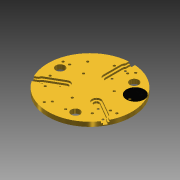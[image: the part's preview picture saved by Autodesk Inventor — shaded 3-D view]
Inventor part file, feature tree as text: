
AUTODESK INVENTOR PART (.ipt)
format: ipt  version: 2014 (Build 180170000, 170)  size: 278,528 bytes
history: native  units: in
note: dims shown in document units (in); Inventor stores cm internally (conversion verified against a paired STEP export)
features: extrude x11, sketch x11, pattern_circular x2, plane x1
ambient origin geometry x8: Origin, YZ Plane, XZ Plane, XY Plane, X Axis, Y Axis, Z Axis, Center Point
bodies: Solid1 (feature_tree)
feature tree (25):
  extrude  "Extrusion1"  Depth=0.25in TaperAngle=0.0deg
  extrude  "Extrusion2"  Depth=0.3in
  extrude  "Extrusion3"  Depth=0.2in TaperAngle=0.0deg
  extrude  "Extrusion4"  Depth=0.1in TaperAngle=0.0deg
  extrude  "Extrusion5"  Depth=0.1in TaperAngle=0.0deg
  extrude  "Extrusion6"  Depth=0.1in TaperAngle=0.0deg
  extrude  "Extrusion8"  Depth=0.25in
  plane  "Work Plane1"
  extrude  "Extrusion11"  Depth=0.1in TaperAngle=0.0deg
  pattern_circular  "Circular Pattern2"  [2 undecoded]
  extrude  "Extrusion12"  Depth=0.002in
  pattern_circular  "Circular Pattern3"  [2 undecoded]
  extrude  "Extrusion13"  Depth=0.002in TaperAngle=360.0deg
  extrude  "Extrusion14"  Depth=0.002in
  sketch  "Sketch1"  dims[d0=4.75in d1=0.25in d2=0.0in]
  sketch  "Sketch2"  dims[d3=1.0in d4=0.3in]
  sketch  "Sketch3"  dims[d5=2.0in d6=0.2in d7=0.0in]
  sketch  "Sketch4"  dims[d8=0.1in d9=0.1in d10=0.0in]
  sketch  "Sketch5"  dims[d11=0.2in d12=0.1in d13=0.0in]
  sketch  "Sketch6"  dims[d14=0.35in d15=0.1in d16=0.0in]
  sketch  "Sketch8"  dims[d17=0.25in d18=0.75in]
  sketch  "Sketch11"  dims[d19=0.12in d20=0.1in d21=0.0in]
  sketch  "Sketch12"  dims[d25=0.5in]
  sketch  "Sketch14"  dims[d26=1.0in]
  sketch  "Sketch15"  dims[d27=0.5in d28=0.025in d29=0.0in d41=0.135in d42=1.0in d43=0.0in d44=1.1811in d45=360.0deg d47=0.75in d48=0.375in d49=0.75in d50=1.0in d51=0.0in d52=2.3622in d53=360.0deg d56=1.0in d60=1.0in d61=0.002in d62=0.0in d63=2.9in d64=0.135in d65=3.0in d66=0.002in d67=0.0in]
note: 4 required parameter values undecoded (feature->parameter linkage not recoverable at this tier; creation-order binding heuristic only, values carry confidence <= 0.55)
